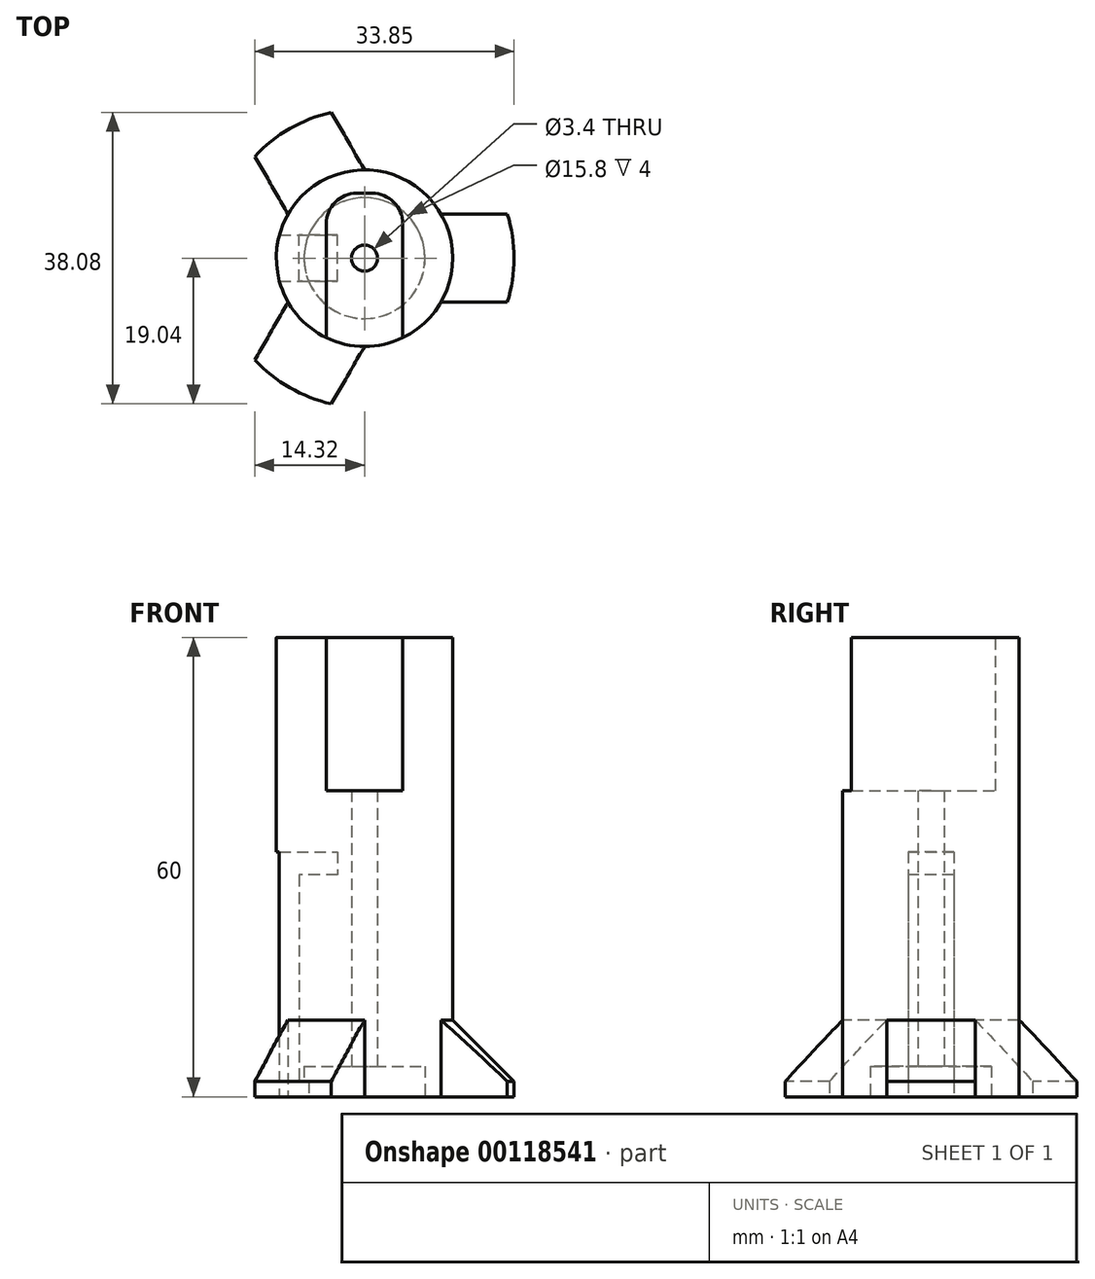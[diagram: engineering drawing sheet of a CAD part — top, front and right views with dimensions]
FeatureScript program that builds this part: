
annotation { "Feature Type Name" : "Feature", "Feature Type Description" : "" }
export const myFeature = defineFeature(function(context is Context, id is Id, definition is map)
    precondition{}
    {
        {
            var Q0;
            Q0=qCreatedBy(makeId("Top.planeOp"),FACE);
            var sketch = newSketch(context, id + "F0", { "sketchPlane" : qUnion([Q0])});
            skCircle(sketch, "E0", {"center": v(0, 0) * mm, "radius": 11.53 * mm});
            skCircle(sketch, "E1", {"center": v(0, 0) * mm, "radius": 9.53 * mm, "construction": true});
            skCircle(sketch, "E2", {"center": v(0, 0) * mm, "radius": 19.53 * mm, "construction": true});
            skLineSegment(sketch, "E3", {"start": v(0, 0) * mm, "end": v(37.52, -21.66) * mm, "construction": true});
            skLineSegment(sketch, "E4", {"start": v(0, 0) * mm, "end": v(33.52, 19.36) * mm, "construction": true});
            skLineSegment(sketch, "E5", {"start": v(0, 0) * mm, "end": v(0, 38.69) * mm, "construction": true});
            skLineSegment(sketch, "E6", {"start": v(0, 0) * mm, "end": v(-30.8, 17.78) * mm, "construction": true});
            skLineSegment(sketch, "E7", {"start": v(0, 0) * mm, "end": v(-26.71, -15.42) * mm, "construction": true});
            skLineSegment(sketch, "E8", {"start": v(0, 0) * mm, "end": v(0, -33.5) * mm, "construction": true});
            skLineSegment(sketch, "E9", {"start": v(0, 0) * mm, "end": v(-17.89, 30.99) * mm, "construction": true});
            skLineSegment(sketch, "E10", {"start": v(0, 0) * mm, "end": v(-16.36, -28.34) * mm, "construction": true});
            skLineSegment(sketch, "E11", {"start": v(18.66, 5.76) * mm, "end": v(9.98, 5.76) * mm});
            skLineSegment(sketch, "E12", {"start": v(18.66, -5.76) * mm, "end": v(9.98, -5.76) * mm});
            skLineSegment(sketch, "E13", {"start": v(-14.32, 13.27) * mm, "end": v(-9.98, 5.76) * mm});
            skLineSegment(sketch, "E14", {"start": v(-4.34, 19.04) * mm, "end": v(0, 11.53) * mm});
            skLineSegment(sketch, "E15", {"start": v(-14.32, -13.27) * mm, "end": v(-9.98, -5.76) * mm});
            skLineSegment(sketch, "E16", {"start": v(0, -11.53) * mm, "end": v(-4.34, -19.04) * mm});
            skArc(sketch, "E17", {"start": v(-14.32, -13.27) * mm, "mid": v(-9.76, -16.9) * mm, "end": v(-4.34, -19.04) * mm});
            skArc(sketch, "E18", {"start": v(-4.34, 19.04) * mm, "mid": v(-9.76, 16.9) * mm, "end": v(-14.32, 13.27) * mm});
            skArc(sketch, "E19", {"start": v(18.66, -5.76) * mm, "mid": v(19.53, 0) * mm, "end": v(18.66, 5.76) * mm});
            skSolve(sketch);
        }
        {
            var Q0;
            {var subQ0=sQuery(id+"F0.wireOp",EDGE,"E11");Q0=makeQuery(id+"F0.imprint","IMPRINT",FACE,{"disambiguationData":[TD([[makeQuery(id+"F0.imprint","IMPRINT",EDGE,{"derivedFrom":subQ0}),1.0]])]});}
            var Q1;
            {var subQ0=sQuery(id+"F0.wireOp",EDGE,"E0");var subQ5=makeQuery(id+"F0.imprint","INTERSECT",VERTEX,{"derivedFrom":[subQ0,sQuery(id+"F0.wireOp",EDGE,"E11")]});Q1=makeQuery(id+"F0.imprint","IMPRINT",FACE,{"disambiguationData":[TD([[makeQuery(id+"F0.imprint","IMPRINT",EDGE,{"disambiguationData":[TD([[subQ5,-1.0]])],"derivedFrom":subQ0}),1.0]])]});}
            var Q2;
            {var subQ0=sQuery(id+"F0.wireOp",EDGE,"E13");Q2=makeQuery(id+"F0.imprint","IMPRINT",FACE,{"disambiguationData":[TD([[makeQuery(id+"F0.imprint","IMPRINT",EDGE,{"derivedFrom":subQ0}),1.0]])]});}
            var Q3;
            {var subQ0=sQuery(id+"F0.wireOp",EDGE,"E15");Q3=makeQuery(id+"F0.imprint","IMPRINT",FACE,{"disambiguationData":[TD([[makeQuery(id+"F0.imprint","IMPRINT",EDGE,{"derivedFrom":subQ0}),-1.0]])]});}
            extrude(context, id + "F1", {"entities" : qUnion([Q0, Q1, Q2, Q3]), "depth" : 10 * mm});
        }
        {
            var Q0;
            Q0=makeQuery(id+"F1.opExtrude","CAP_EDGE",EDGE,{"disambiguationData":[OSD([sQuery(id+"F0.wireOp",EDGE,"E19")])],"isStart":false});
            var Q1;
            Q1=makeQuery(id+"F1.opExtrude","CAP_EDGE",EDGE,{"disambiguationData":[OSD([sQuery(id+"F0.wireOp",EDGE,"E17")])],"isStart":false});
            var Q2;
            Q2=makeQuery(id+"F1.opExtrude","CAP_EDGE",EDGE,{"disambiguationData":[OSD([sQuery(id+"F0.wireOp",EDGE,"E18")])],"isStart":false});
            chamfer(context, id + "F2", {"entities" : qUnion([Q0, Q1, Q2]), "width" : 8 * mm, "tangentPropagation" : true});
        }
        {
            var Q0;
            Q0=makeQuery(id+"F1.opExtrude","CAP_FACE",FACE,{"disambiguationData":[OSD([sQuery(id+"F0.wireOp",EDGE,"E0"),sQuery(id+"F0.wireOp",EDGE,"E11"),sQuery(id+"F0.wireOp",EDGE,"E12"),sQuery(id+"F0.wireOp",EDGE,"E13"),sQuery(id+"F0.wireOp",EDGE,"E14"),sQuery(id+"F0.wireOp",EDGE,"E15"),sQuery(id+"F0.wireOp",EDGE,"E16"),sQuery(id+"F0.wireOp",EDGE,"E17"),sQuery(id+"F0.wireOp",EDGE,"E18"),sQuery(id+"F0.wireOp",EDGE,"E19")])],"isStart":false});
            var sketch = newSketch(context, id + "F3", { "sketchPlane" : qUnion([Q0])});
            skCircle(sketch, "E20", {"center": v(0, 0) * mm, "radius": 11.53 * mm});
            skSolve(sketch);
        }
        {
            var Q0;
            {var subQ0=sQuery(id+"F3.wireOp",EDGE,"E20");var subQ4=makeQuery(id+"F3.imprint","IMPRINT",VERTEX,{"disambiguationData":[OD(2.0)],"derivedFrom":subQ0});Q0=makeQuery(id+"F3.imprint","IMPRINT",FACE,{"disambiguationData":[TD([[makeQuery(id+"F3.imprint","IMPRINT",EDGE,{"disambiguationData":[TD([[subQ4,1.0]])],"derivedFrom":subQ0}),1.0]])]});}
            extrude(context, id + "F4", {"entities" : qUnion([Q0]), "operationType" : NewBodyOperationType.ADD, "depth" : 50 * mm});
        }
        {
            var Q0;
            Q0=makeQuery(id+"F1.opExtrude","CAP_FACE",FACE,{"disambiguationData":[OSD([sQuery(id+"F0.wireOp",EDGE,"E0"),sQuery(id+"F0.wireOp",EDGE,"E11"),sQuery(id+"F0.wireOp",EDGE,"E12"),sQuery(id+"F0.wireOp",EDGE,"E13"),sQuery(id+"F0.wireOp",EDGE,"E14"),sQuery(id+"F0.wireOp",EDGE,"E15"),sQuery(id+"F0.wireOp",EDGE,"E16"),sQuery(id+"F0.wireOp",EDGE,"E17"),sQuery(id+"F0.wireOp",EDGE,"E18"),sQuery(id+"F0.wireOp",EDGE,"E19")])],"isStart":true});
            var sketch = newSketch(context, id + "F5", { "sketchPlane" : qUnion([Q0])});
            skCircle(sketch, "E21", {"center": v(0, 0) * mm, "radius": 10.67 * mm, "construction": true});
            skCircle(sketch, "E22", {"center": v(0, 0) * mm, "radius": 7.9 * mm});
            skSolve(sketch);
        }
        {
            var Q0;
            Q0=makeQuery(id+"F5.imprint","IMPRINT",FACE,{"disambiguationData":[TD([[makeQuery(id+"F5.imprint","IMPRINT",EDGE,{"derivedFrom":sQuery(id+"F5.wireOp",EDGE,"E22")}),1.0]])]});
            extrude(context, id + "F6", {"entities" : qUnion([Q0]), "operationType" : NewBodyOperationType.REMOVE, "oppositeDirection" : true, "depth" : 4 * mm});
        }
        {
            var Q0;
            Q0=makeQuery(id+"F1.opExtrude","CAP_FACE",FACE,{"disambiguationData":[OSD([sQuery(id+"F0.wireOp",EDGE,"E0"),sQuery(id+"F0.wireOp",EDGE,"E11"),sQuery(id+"F0.wireOp",EDGE,"E12"),sQuery(id+"F0.wireOp",EDGE,"E13"),sQuery(id+"F0.wireOp",EDGE,"E14"),sQuery(id+"F0.wireOp",EDGE,"E15"),sQuery(id+"F0.wireOp",EDGE,"E16"),sQuery(id+"F0.wireOp",EDGE,"E17"),sQuery(id+"F0.wireOp",EDGE,"E18"),sQuery(id+"F0.wireOp",EDGE,"E19")])],"isStart":true});
            var sketch = newSketch(context, id + "F7", { "sketchPlane" : qUnion([Q0])});
            skLineSegment(sketch, "E23", {"start": v(-11.13, 3) * mm, "end": v(-7.3, 3) * mm});
            skLineSegment(sketch, "E24", {"start": v(-11.13, -3) * mm, "end": v(-7.3, -3) * mm});
            skArc(sketch, "E25", {"start": v(-11.13, 3) * mm, "mid": v(-11.52, 0) * mm, "end": v(-11.13, -3) * mm});
            skArc(sketch, "E26", {"start": v(-7.3, 3) * mm, "mid": v(-7.9, 0) * mm, "end": v(-7.3, -3) * mm});
            skSolve(sketch);
        }
        {
            var Q0;
            Q0=makeQuery(id+"F7.imprint","IMPRINT",FACE,{"disambiguationData":[TD([[makeQuery(id+"F7.imprint","IMPRINT",EDGE,{"derivedFrom":sQuery(id+"F7.wireOp",EDGE,"E23")}),-1.0]])]});
            extrude(context, id + "F8", {"entities" : qUnion([Q0]), "operationType" : NewBodyOperationType.REMOVE, "oppositeDirection" : true, "depth" : 2 * mm});
        }
        {
            var Q0;
            Q0=makeQuery(id+"F8.boolean.opBoolean","COPY",FACE,{"derivedFrom":makeQuery(id+"F8.opExtrude","CAP_FACE",FACE,{"disambiguationData":[OSD([sQuery(id+"F7.wireOp",EDGE,"E23"),sQuery(id+"F7.wireOp",EDGE,"E24"),sQuery(id+"F7.wireOp",EDGE,"E25"),sQuery(id+"F7.wireOp",EDGE,"E26")])],"isStart":false})});
            var sketch = newSketch(context, id + "F9", { "sketchPlane" : qUnion([Q0])});
            skLineSegment(sketch, "E27", {"start": v(-8.53, 3) * mm, "end": v(-8.53, -3) * mm});
            skSolve(sketch);
        }
        {
            var Q0;
            {var subQ0=sQuery(id+"F9.wireOp",EDGE,"E27");Q0=makeQuery(id+"F9.imprint","IMPRINT",FACE,{"disambiguationData":[TD([[makeQuery(id+"F9.imprint","IMPRINT",EDGE,{"derivedFrom":subQ0}),-1.0]])]});}
            extrude(context, id + "F10", {"entities" : qUnion([Q0]), "operationType" : NewBodyOperationType.REMOVE, "oppositeDirection" : true, "depth" : 30 * mm});
        }
        {
            var Q0;
            Q0=makeQuery(id+"F10.boolean.opBoolean","COPY",FACE,{"derivedFrom":makeQuery(id+"F10.opExtrude","SWEPT_FACE",FACE,{"disambiguationData":[OSD([sQuery(id+"F9.wireOp",EDGE,"E27")])]})});
            var sketch = newSketch(context, id + "F11", { "sketchPlane" : qUnion([Q0])});
            skLineSegment(sketch, "E28", {"start": v(-3, 29) * mm, "end": v(3, 29) * mm});
            skSolve(sketch);
        }
        {
            var Q0;
            {var subQ0=sQuery(id+"F11.wireOp",EDGE,"E28");Q0=makeQuery(id+"F11.imprint","IMPRINT",FACE,{"disambiguationData":[TD([[makeQuery(id+"F11.imprint","IMPRINT",EDGE,{"derivedFrom":subQ0}),1.0]])]});}
            extrude(context, id + "F12", {"entities" : qUnion([Q0]), "operationType" : NewBodyOperationType.REMOVE, "oppositeDirection" : true, "depth" : 5 * mm});
        }
        {
            var Q0;
            Q0=makeQuery(id+"F6.boolean.opBoolean","COPY",FACE,{"derivedFrom":makeQuery(id+"F6.opExtrude","CAP_FACE",FACE,{"disambiguationData":[OSD([sQuery(id+"F5.wireOp",EDGE,"E22")])],"isStart":false})});
            var sketch = newSketch(context, id + "F13", { "sketchPlane" : qUnion([Q0])});
            skCircle(sketch, "E29", {"center": v(0, 0) * mm, "radius": 1.7 * mm});
            skSolve(sketch);
        }
        {
            var Q0;
            Q0=makeQuery(id+"F13.imprint","IMPRINT",FACE,{"disambiguationData":[TD([[makeQuery(id+"F13.imprint","IMPRINT",EDGE,{"derivedFrom":sQuery(id+"F13.wireOp",EDGE,"E29")}),1.0]])]});
            extrude(context, id + "F14", {"entities" : qUnion([Q0]), "operationType" : NewBodyOperationType.REMOVE, "endBound" : BoundingType.UP_TO_NEXT, "oppositeDirection" : true, "depth" : 25.4 * mm});
        }
        {
            var Q0;
            Q0=makeQuery(id+"F4.opExtrude","CAP_FACE",FACE,{"disambiguationData":[OSD([sQuery(id+"F3.wireOp",EDGE,"E20")])],"isStart":false});
            var sketch = newSketch(context, id + "F15", { "sketchPlane" : qUnion([Q0])});
            skLineSegment(sketch, "E30", {"start": v(-5, -10.38) * mm, "end": v(-5, 8.47) * mm});
            skLineSegment(sketch, "E31", {"start": v(-5, 8.47) * mm, "end": v(5, 8.47) * mm});
            skLineSegment(sketch, "E32", {"start": v(5, 8.47) * mm, "end": v(5, -10.38) * mm});
            skSolve(sketch);
        }
        {
            var Q0;
            {var subQ2=sQuery(id+"F15.wireOp",EDGE,"E30");Q0=makeQuery(id+"F15.imprint","IMPRINT",FACE,{"disambiguationData":[TD([[makeQuery(id+"F15.imprint","IMPRINT",EDGE,{"derivedFrom":subQ2}),-1.0]])]});}
            extrude(context, id + "F16", {"entities" : qUnion([Q0]), "operationType" : NewBodyOperationType.REMOVE, "oppositeDirection" : true, "depth" : 20 * mm});
        }
        {
            var Q0;
            Q0=makeQuery(id+"F16.boolean.opBoolean","COPY",EDGE,{"derivedFrom":makeQuery(id+"F16.opExtrude","SWEPT_EDGE",EDGE,{"disambiguationData":[OSD([sQuery(id+"F15.wireOp",EDGE,"E30"),sQuery(id+"F15.wireOp",EDGE,"E31")])]})});
            var Q1;
            Q1=makeQuery(id+"F16.boolean.opBoolean","COPY",EDGE,{"derivedFrom":makeQuery(id+"F16.opExtrude","SWEPT_EDGE",EDGE,{"disambiguationData":[OSD([sQuery(id+"F15.wireOp",EDGE,"E31"),sQuery(id+"F15.wireOp",EDGE,"E32")])]})});
            fillet(context, id + "F17", {"entities" : qUnion([Q0, Q1]), "radius" : 4 * mm, "tangentPropagation" : true, "allowEdgeOverflow" : false});
        }
    });
